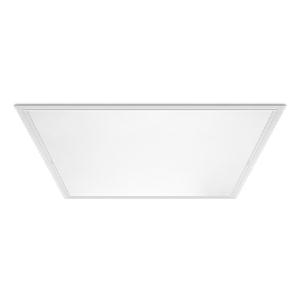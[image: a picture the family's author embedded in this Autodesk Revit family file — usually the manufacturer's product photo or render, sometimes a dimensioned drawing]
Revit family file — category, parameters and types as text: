
# Revit family: 3f_filippi_-_l_340_luce_diffusa_vs_ip65v_3f_filippi_-_23926_-_l_340_45w-940_dali_vs_ip65v_596x596
name_source: partatom
category: Lighting Fixtures
units: mm (PartAtom-declared; Revit-internal decimal feet)

## family parameters
Cut with Voids When Loaded = No
Host = Face
Light Source = No
Part Type = Normal
Room Calculation Point = No
Round Connector Dimension = Use Diameter
Shared = No

## types (1)
- 3F Filippi - L 340 Luce Diffusa VS IP65V (1 x LED, 4684 lm, 52 W, 4000 K)
    Apparent Load = 52 VA
    Approval mark = ENEC
    CIE Flux Codes = 61 89 98 100 100
    Color Rendering = 90
    Color Temperature = 4000 K
    Control Gear = Electronic transformer
    Default Elevation = 1800 mm
    Description = ILLUMINOTECHNICAL
Luminous efficiency 100% (DLOR 100%, ULOR 0%).
Initial luminous flux of the luminaire 4684 lm.
Direct symmetric distribution.
Installation Interdistance Transv.D = 1.17 x hu - Long.D = 1.14 x hu.
Average luminance <3000 cd/m² for radial angles >65°.
Tabular UGR (CIE 117 - 4H-8H; S=0.25H; 70/50/20): RUG 18.6 - 18.4.
Beam angle: 91° - 88°.
Luminous efficacy 90 lm/W.
Lifetime (L93/B10): 30000 h. (tq+25°C)
Lifetime (L90/B10): 50000 h. (tq+25°C)
Lifetime (L85/B10): 80000 h. (tq+25°C)
Lifetime (L80/B10): 100000 h. (tq+25°C)
Sudden decreased luminous flux after 50000 hours: 0% (C0).
Photobiological safety in compliance with IEC/TR 62778: RG0 risk exempt, (IEC 62471).
In compliance with IEC/EN 62722-2-1 - IEC/EN 62717 standards.

SOURCE
Squared LED module 45W/940.
Energy efficiency class (UE 2019/2020 - UE 2019/2015): D.
CIE 13.3 Colour rendering index: CRI >90 (R9 >50%).
IES TM-30 Fidelity Index: Rf = 92 Rg = 101.
CCT nominal colour temperature 4000 K.
Colour initial tolerance (MacAdam): SDCM 3.

MECHANICAL
Housing in hot-galvanised steel, painted in white polyester.
Perimetral frame in white polycarbonate.
VS moulded glass, anti-glare, tempered, non-combustible, thickness 4 mm.
Luminaire with limited surface temperature. - D - (EN 60598-2-24)
Dimensions: 596x596 mm, height 80 mm. Weight 6.4 kg.
IP65 protection degree for exposed part, IP40 for recessed part.
Mechanical strength to impacts IK08 (5 joule).
Glow-wire test resistance 960°C.

ELECTRICAL
Wiring on a separate unit.
Halogen Free DALI-2 DATI (Parts 251, 252, 253), PUSH-DIM, electronic wiring 230V-50/60Hz, power factor 0.95 at full load, THD <25%, constant output current, SELV, class II, 1 driver, 1 DALI addresse.
Power of the luminaire 52 W.
CE - IEC 60598-1 - EN 60598-1.
SAFE FLICKER: PstLM=<1 and SVM=<0.4 (IEC TR 61547-1 and IEC TR 63158), to ensure a more comfortable and safe light.
Luminaire compliant with EN 60598-2-22 for power supply from a centralised emergency system CPSS (Central Power Supply System), not incorporated in the luminaire - high risk areas excluded. The default power and flux are 100% in AC and 15% in DC.
Ambient temperature from 0°C to +40°C.
Temperature class T6 max 85°C.
Relative humidity UR: <85%.

INSTALLATION
Lay-on or pull-up recessed fitting using frame and anti-fall safety cable accessories.
All accessories dedicated to this product are available on the Catalog and on our website www.3F-Filippi.com.

APPLICATIONS
In environments requiring protection and simplified cleaning.
Hospitals, pharmaceutical, chemical, aseptic laboratories, sterilised rooms.
Environments: with VDTs, meeting rooms, offices.
Environments: architectural, commercial, staterooms, banks.
Environments where demanding visual tasks are performed and soft diffuse light is required for optimal visual comfort and total shielding of the light source.

LIGHT MANAGEMENT
Recommended minimum setting: 10%.
The luminaire, equipped with (DALI-2 DATI) driver, can be controlled manually with 3F Easy Dim technology or automatically/manually with wired or wireless DALI/D2D control systems.
The D2D driver guarantees interoperability with other devices with the same certification by making the following information available:
Device Data (Part 251), Energy Report (Part 252), Diagnosis & Maintenance (Part 253).
In electrical systems without a regulation system (manual or automatic) and DALI bus, a suitable jumper must be made on the DA-DA terminals of the appliance.

WARNING
Luminaire designed for disposal/recycling at end-of-life.
Replaceable (LED only) light source by a professional. Replaceable control gear by a professional.
    Height = 0 mm  [stored 0 ft]
    Lamp = 1 x LED
    Lamp Light Flux = 4684 lm
    Lamp Power = 52 W
    Lamp count = 1
    Length = 596 mm
    Lifetime = 50000 h
    Luminous efficacy = 90 lm/W
    Manufacturer = 3F Filippi
    ModVariant = No
    Model = 3F Filippi - 23926 - L 340 45W-940 DALI VS IP65V 596x596
    Mounting Place = Ceiling
    Mounting Type = Recessed
    Number of Poles = 1
    OnlyDefault = Yes
    Power Factor = 1
    Product Name = 3F Filippi - L 340 Luce Diffusa VS IP65V
    Product group = recessed luminaire
    ProductGroupID = 4
    Protection Class = Protection class II
    Protection Degree = IP 40
    RLX_Detail_Level = 1
    RLX_Emergency_Light_Flux = 0 lm
    RLX_Emergency_Type = 0
    RLX_Emergency_Type_DB = No
    RlxData = <blob elided: 155541 chars, md5=4989cab9>
    Socket = socket
    Standby Power = 0 W
    System Light Flux = 4684 lm
    System Power = 52 W
    Type Comments = Product without accessories
    Type Image = 3ffilippi_l_340_luce_diffusa_vs.jpg
    URL = http://relux.com
    VarID = ---
    Voltage = 0 V
    Weight = 0.00 kg
    Width = 596 mm

note: [stored X ft] marks values corroborated as IEEE doubles in the binary element streams (Revit-internal decimal feet)

## geometry (parser evidence)
native form markers: Blend x4, Sweep x9
no freeform markers — native parametric forms only
